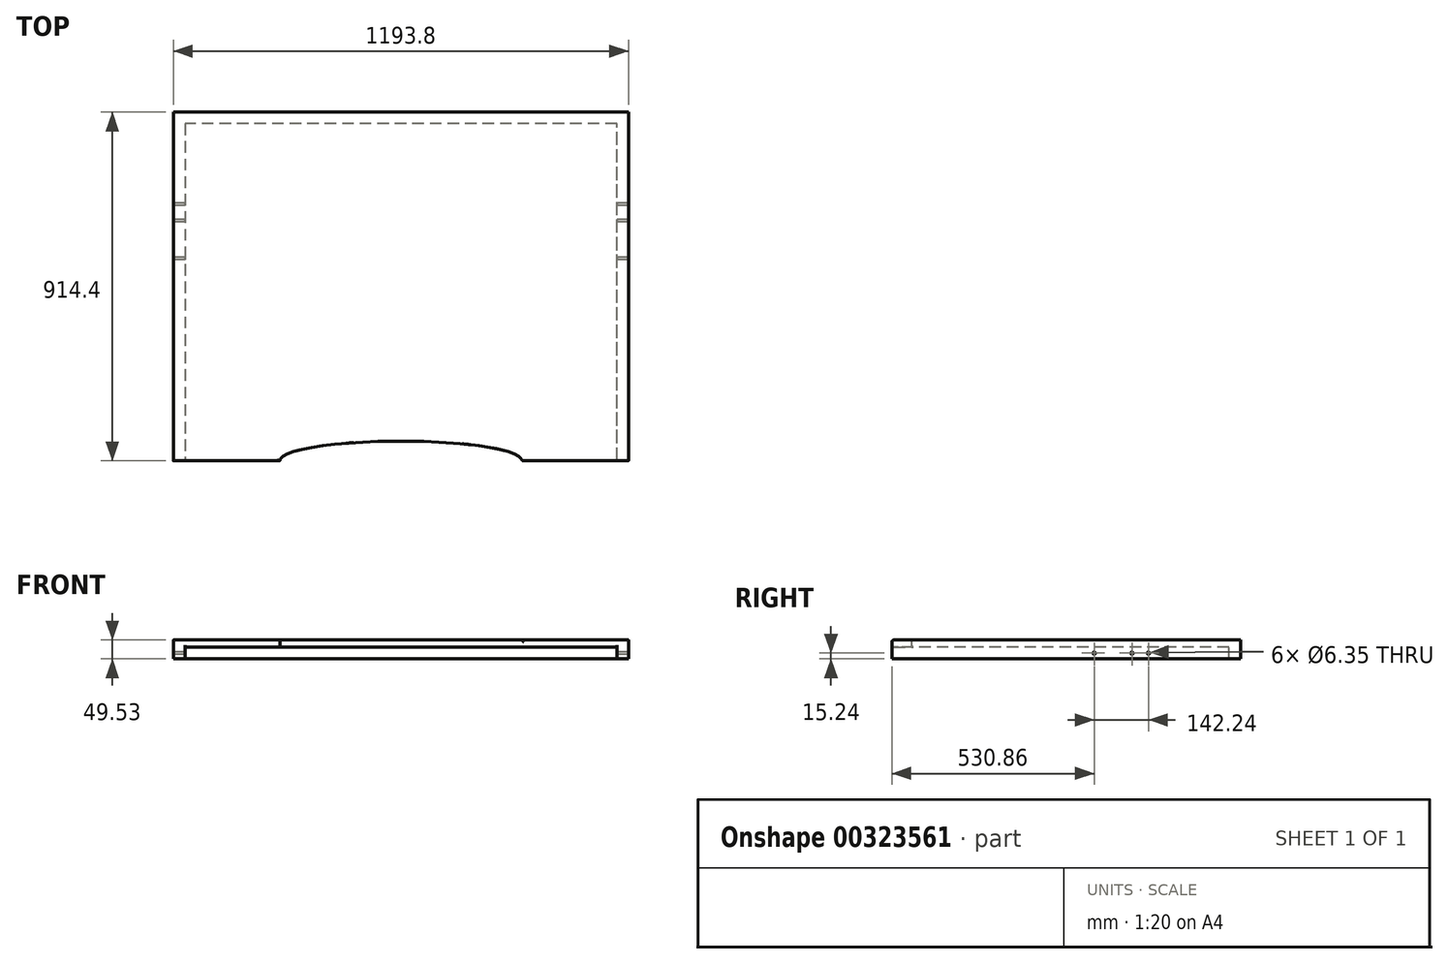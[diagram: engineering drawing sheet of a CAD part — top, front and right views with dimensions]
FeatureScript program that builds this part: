
annotation { "Feature Type Name" : "Feature", "Feature Type Description" : "" }
export const myFeature = defineFeature(function(context is Context, id is Id, definition is map)
    precondition{}
    {
        {
            var Q0;
            Q0=qCreatedBy(makeId("Top.planeOp"),FACE);
            var sketch = newSketch(context, id + "F0", { "sketchPlane" : qUnion([Q0])});
            skLineSegment(sketch, "E0.bottom", {"start": v(-596.9, 457.2) * mm, "end": v(596.9, 457.2) * mm});
            skLineSegment(sketch, "E0.top", {"start": v(-596.9, -457.2) * mm, "end": v(596.9, -457.2) * mm});
            skLineSegment(sketch, "E0.left", {"start": v(-596.9, 457.2) * mm, "end": v(-596.9, -457.2) * mm});
            skLineSegment(sketch, "E0.right", {"start": v(596.9, 457.2) * mm, "end": v(596.9, -457.2) * mm});
            skPoint(sketch, "E0.middle", {"position": v(0, 0) * mm});
            skSolve(sketch);
        }
        {
            var Q0;
            Q0=makeQuery(id+"F0.imprint","IMPRINT",FACE,{"disambiguationData":[TD([[makeQuery(id+"F0.imprint","IMPRINT",EDGE,{"derivedFrom":sQuery(id+"F0.wireOp",EDGE,"E0.bottom")}),-1.0]])]});
            extrude(context, id + "F1", {"entities" : qUnion([Q0]), "depth" : 19.05 * mm});
        }
        {
            var Q0;
            Q0=makeQuery(id+"F1.opExtrude","CAP_FACE",FACE,{"disambiguationData":[OSD([sQuery(id+"F0.wireOp",EDGE,"E0.bottom"),sQuery(id+"F0.wireOp",EDGE,"E0.top"),sQuery(id+"F0.wireOp",EDGE,"E0.left"),sQuery(id+"F0.wireOp",EDGE,"E0.right")])],"isStart":true});
            var sketch = newSketch(context, id + "F2", { "sketchPlane" : qUnion([Q0])});
            skLineSegment(sketch, "E1.bottom", {"start": v(-596.9, -457.2) * mm, "end": v(-566.42, -457.2) * mm});
            skLineSegment(sketch, "E1.top", {"start": v(-596.9, 457.2) * mm, "end": v(-566.42, 457.2) * mm});
            skLineSegment(sketch, "E1.left", {"start": v(-596.9, -457.2) * mm, "end": v(-596.9, 457.2) * mm});
            skLineSegment(sketch, "E1.right", {"start": v(-566.42, -457.2) * mm, "end": v(-566.42, 457.2) * mm});
            skLineSegment(sketch, "E2.bottom", {"start": v(596.9, -457.2) * mm, "end": v(-566.42, -457.2) * mm});
            skLineSegment(sketch, "E2.top", {"start": v(596.9, -426.72) * mm, "end": v(-566.42, -426.72) * mm});
            skLineSegment(sketch, "E2.left", {"start": v(596.9, -457.2) * mm, "end": v(596.9, -426.72) * mm});
            skLineSegment(sketch, "E2.right", {"start": v(-566.42, -457.2) * mm, "end": v(-566.42, -426.72) * mm});
            skLineSegment(sketch, "E3.bottom", {"start": v(596.9, 457.2) * mm, "end": v(566.42, 457.2) * mm});
            skLineSegment(sketch, "E3.top", {"start": v(596.9, -426.72) * mm, "end": v(566.42, -426.72) * mm});
            skLineSegment(sketch, "E3.left", {"start": v(596.9, 457.2) * mm, "end": v(596.9, -426.72) * mm});
            skLineSegment(sketch, "E3.right", {"start": v(566.42, 457.2) * mm, "end": v(566.42, -426.72) * mm});
            skSolve(sketch);
        }
        {
            var Q0;
            Q0 = qSketchRegion(id + "F2", true);
            extrude(context, id + "F3", {"entities" : qUnion([Q0]), "operationType" : NewBodyOperationType.ADD, "depth" : 30.48 * mm});
        }
        {
            var Q0;
            Q0=makeQuery(id+"F3.opExtrude","SWEPT_FACE",FACE,{"disambiguationData":[OSD([sQuery(id+"F2.wireOp",EDGE,"E1.left")])]});
            var sketch = newSketch(context, id + "F4", { "sketchPlane" : qUnion([Q0])});
            skPoint(sketch, "E4", {"position": v(-215.9, -15.24) * mm});
            skPoint(sketch, "E5", {"position": v(-172.72, -15.24) * mm});
            skPoint(sketch, "E6", {"position": v(-73.66, -15.24) * mm});
            skSolve(sketch);
        }
        {
            var Q0;
            Q0=sQuery(id+"F4.wireOp",VERTEX,"E4");
            var Q1;
            Q1=sQuery(id+"F4.wireOp",VERTEX,"E5");
            var Q2;
            Q2=sQuery(id+"F4.wireOp",VERTEX,"E6");
            var Q3;
            Q3=makeQuery(id+"F1.opExtrude","SWEPT_BODY",BODY,{"disambiguationData":[OSD([sQuery(id+"F0.wireOp",EDGE,"E0.bottom"),sQuery(id+"F0.wireOp",EDGE,"E0.top"),sQuery(id+"F0.wireOp",EDGE,"E0.left"),sQuery(id+"F0.wireOp",EDGE,"E0.right")])]});
            hole(context, id + "F5", {"style" : HoleStyle.SIMPLE, "endStyle" : HoleEndStyle.THROUGH, "holeDiameter" : 6.35 * mm, "tappedDepth" : 12.7 * mm, "tapClearance" : 3, "locations" : qUnion([Q0, Q1, Q2]), "scope" : qUnion([Q3])});
        }
        {
            var Q0;
            Q0=makeQuery(id+"F1.opExtrude","CAP_FACE",FACE,{"disambiguationData":[OSD([sQuery(id+"F0.wireOp",EDGE,"E0.bottom"),sQuery(id+"F0.wireOp",EDGE,"E0.top"),sQuery(id+"F0.wireOp",EDGE,"E0.left"),sQuery(id+"F0.wireOp",EDGE,"E0.right")])],"isStart":false});
            var sketch = newSketch(context, id + "F6", { "sketchPlane" : qUnion([Q0])});
            skEllipse(sketch, "E7", {"center": v(0, -457.2) * mm, "majorRadius": 317.5 * mm, "minorRadius": 51.67 * mm, "majorAxis": v(-1, 0)});
            skSolve(sketch);
        }
        {
            var Q0;
            {var subQ0=sQuery(id+"F6.wireOp",EDGE,"E7");var subQ1=makeQuery(id+"F1.opExtrude","CAP_EDGE",EDGE,{"disambiguationData":[OSD([sQuery(id+"F0.wireOp",EDGE,"E0.top")])],"isStart":false});var subQ2=makeQuery(id+"F6.imprint","INTERSECT",VERTEX,{"disambiguationData":[OD(0.0)],"derivedFrom":[subQ1,subQ0]});Q0=makeQuery(id+"F6.imprint","IMPRINT",FACE,{"disambiguationData":[TD([[makeQuery(id+"F6.imprint","IMPRINT",EDGE,{"disambiguationData":[TD([[subQ2,1.0]])],"derivedFrom":subQ0}),1.0]])]});}
            extrude(context, id + "F7", {"entities" : qUnion([Q0]), "operationType" : NewBodyOperationType.REMOVE, "oppositeDirection" : true, "depth" : 38.1 * mm});
        }
        {
            var Q0;
            {var subQ0=sQuery(id+"F0.wireOp",EDGE,"E0.left");var subQ1=sQuery(id+"F0.wireOp",EDGE,"E0.top");Q0=makeQuery(id+"F7.boolean.opBoolean","SPLIT",EDGE,{"disambiguationData":[TD([makeQuery(id+"F1.opExtrude","SWEPT_FACE",FACE,{"disambiguationData":[OSD([subQ0])]})])],"derivedFrom":makeQuery(id+"F1.opExtrude","CAP_EDGE",EDGE,{"disambiguationData":[OSD([subQ1])],"isStart":false})});}
            var Q1;
            Q1=makeQuery(id+"F7.boolean.opBoolean","COPY",EDGE,{"derivedFrom":makeQuery(id+"F7.opExtrude","CAP_EDGE",EDGE,{"disambiguationData":[OSD([sQuery(id+"F6.wireOp",EDGE,"E7")])],"isStart":true})});
            var Q2;
            {var subQ0=sQuery(id+"F0.wireOp",EDGE,"E0.right");var subQ1=sQuery(id+"F0.wireOp",EDGE,"E0.top");Q2=makeQuery(id+"F7.boolean.opBoolean","SPLIT",EDGE,{"disambiguationData":[TD([makeQuery(id+"F1.opExtrude","SWEPT_FACE",FACE,{"disambiguationData":[OSD([subQ0])]})])],"derivedFrom":makeQuery(id+"F1.opExtrude","CAP_EDGE",EDGE,{"disambiguationData":[OSD([subQ1])],"isStart":false})});}
            var Q3;
            {var subQ0=sQuery(id+"F0.wireOp",EDGE,"E0.top");Q3=makeQuery(id+"F7.boolean.opBoolean","SPLIT",EDGE,{"disambiguationData":[TD([makeQuery(id+"F3.opExtrude","SWEPT_FACE",FACE,{"disambiguationData":[OSD([sQuery(id+"F2.wireOp",EDGE,"E3.right")])]})])],"derivedFrom":makeQuery(id+"F1.opExtrude","CAP_EDGE",EDGE,{"disambiguationData":[OSD([subQ0])],"isStart":true})});}
            var Q4;
            Q4=makeQuery(id+"F7.boolean.opBoolean","INTERSECT",EDGE,{"derivedFrom":[makeQuery(id+"F1.opExtrude","CAP_FACE",FACE,{"disambiguationData":[OSD([sQuery(id+"F0.wireOp",EDGE,"E0.bottom"),sQuery(id+"F0.wireOp",EDGE,"E0.top"),sQuery(id+"F0.wireOp",EDGE,"E0.left"),sQuery(id+"F0.wireOp",EDGE,"E0.right")])],"isStart":true}),makeQuery(id+"F7.opExtrude","SWEPT_FACE",FACE,{"disambiguationData":[OSD([sQuery(id+"F6.wireOp",EDGE,"E7")])]})]});
            var Q5;
            {var subQ0=sQuery(id+"F0.wireOp",EDGE,"E0.top");Q5=makeQuery(id+"F7.boolean.opBoolean","SPLIT",EDGE,{"disambiguationData":[TD([makeQuery(id+"F3.opExtrude","SWEPT_FACE",FACE,{"disambiguationData":[OSD([sQuery(id+"F2.wireOp",EDGE,"E1.right")])]})])],"derivedFrom":makeQuery(id+"F1.opExtrude","CAP_EDGE",EDGE,{"disambiguationData":[OSD([subQ0])],"isStart":true})});}
            var Q6;
            {var subQ0=sQuery(id+"F6.wireOp",EDGE,"E7");var subQ1=sQuery(id+"F0.wireOp",EDGE,"E0.top");Q6=makeQuery(id+"F7.boolean.opBoolean","COPY",EDGE,{"derivedFrom":makeQuery(id+"F7.opExtrude","SWEPT_EDGE",EDGE,{"disambiguationData":[OSD([subQ1,subQ0]),TDD([makeQuery(id+"F6.imprint","INTERSECT",VERTEX,{"disambiguationData":[OD(0.0)],"derivedFrom":[makeQuery(id+"F1.opExtrude","CAP_EDGE",EDGE,{"disambiguationData":[OSD([subQ1])],"isStart":false}),subQ0]})])]})});}
            var Q7;
            {var subQ0=sQuery(id+"F6.wireOp",EDGE,"E7");var subQ1=sQuery(id+"F0.wireOp",EDGE,"E0.top");Q7=makeQuery(id+"F7.boolean.opBoolean","COPY",EDGE,{"derivedFrom":makeQuery(id+"F7.opExtrude","SWEPT_EDGE",EDGE,{"disambiguationData":[OSD([subQ1,subQ0]),TDD([makeQuery(id+"F6.imprint","INTERSECT",VERTEX,{"disambiguationData":[OD(1.0)],"derivedFrom":[makeQuery(id+"F1.opExtrude","CAP_EDGE",EDGE,{"disambiguationData":[OSD([subQ1])],"isStart":false}),subQ0]})])]})});}
            fillet(context, id + "F8", {"entities" : qUnion([Q0, Q1, Q2, Q3, Q4, Q5, Q6, Q7]), "radius" : 5.08 * mm, "tangentPropagation" : true, "allowEdgeOverflow" : false});
        }
    });
